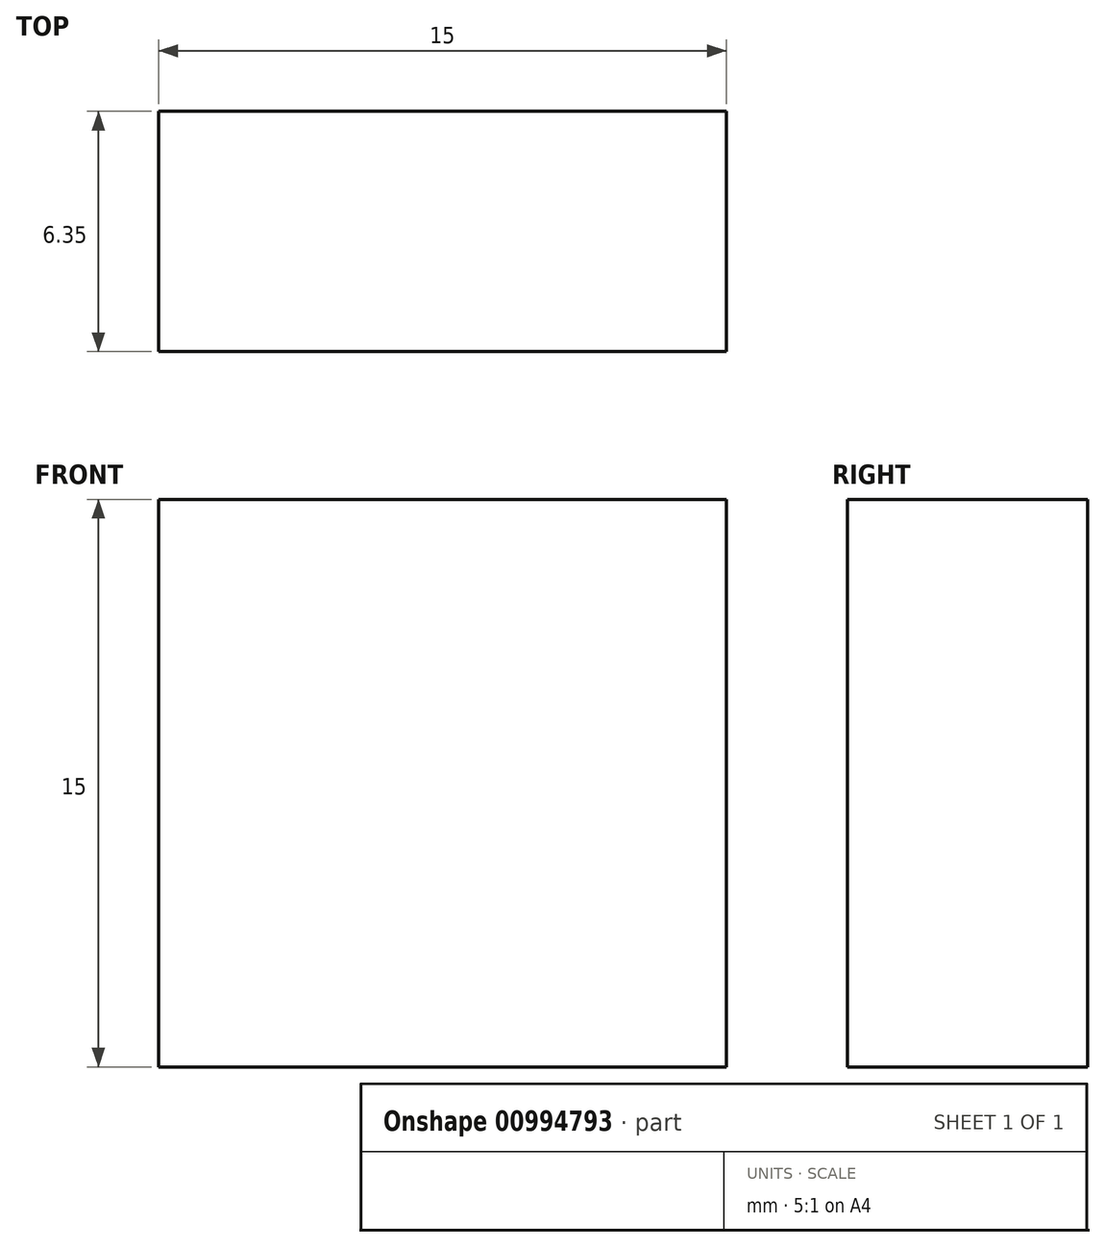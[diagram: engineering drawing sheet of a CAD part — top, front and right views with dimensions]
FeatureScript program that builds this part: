
annotation { "Feature Type Name" : "Feature", "Feature Type Description" : "" }
export const myFeature = defineFeature(function(context is Context, id is Id, definition is map)
    precondition{}
    {
        {
            var Q0;
            Q0=qCreatedBy(makeId("Front.planeOp"),FACE);
            var sketch = newSketch(context, id + "F0", { "sketchPlane" : qUnion([Q0])});
            skLineSegment(sketch, "E0.bottom", {"start": v(-7.5, -7.5) * mm, "end": v(7.5, -7.5) * mm});
            skLineSegment(sketch, "E0.top", {"start": v(-7.5, 7.5) * mm, "end": v(7.5, 7.5) * mm});
            skLineSegment(sketch, "E0.left", {"start": v(-7.5, -7.5) * mm, "end": v(-7.5, 7.5) * mm});
            skLineSegment(sketch, "E0.right", {"start": v(7.5, -7.5) * mm, "end": v(7.5, 7.5) * mm});
            skPoint(sketch, "E0.middle", {"position": v(0, 0) * mm});
            skSolve(sketch);
        }
        {
            var Q0;
            Q0 = qSketchRegion(id + "F0", true);
            extrude(context, id + "F1", {"entities" : qUnion([Q0]), "depth" : 6.35 * mm, "offsetDistance" : 25.4 * mm});
        }
    });
